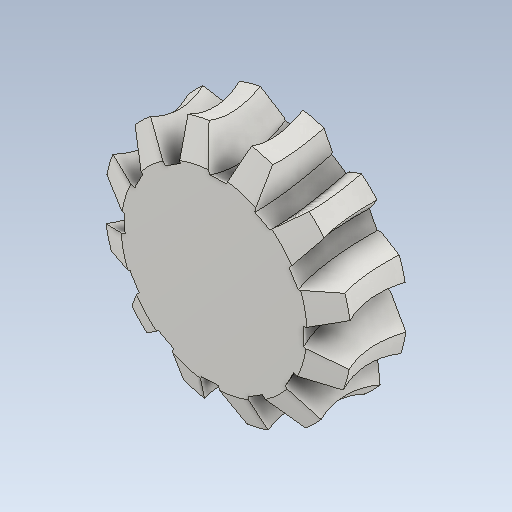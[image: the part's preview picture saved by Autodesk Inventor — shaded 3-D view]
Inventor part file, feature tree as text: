
AUTODESK INVENTOR PART (.ipt)
format: ipt  version: 2021 (Build 250183000, 183)  size: 323,072 bytes
history: native  units: mm (DEFAULTED — no unit token found)
features: other x8, plane x3, pattern_circular x1, sketch x1
ambient origin geometry x5: Origin, X Axis, Y Axis, Z Axis, Center Point
bodies: Solid1 (feature_tree)
feature tree (13):
  other  "Tooth Plane"
  other  "Base Body Sketch"
  other  "Base Body"
  other  "Base Body2"
  plane  "Work Plane13"
  other  "Tooth"
  pattern_circular  "Tooth Pattern"  [2 undecoded]
  plane  "Work Plane14"
  plane  "Work Plane15"
  other  "Tooth Sketch"
  sketch  "Sketch8"  dims[d35=90.0deg d37=-0.996687mm d38=44.0mm d39=3.490659mm d40=15.2mm d41=20.0mm d42=3.769911mm d43=90.0deg d44=120.0mm d46=360.0deg d50=4.297754mm d68=44.0mm d69=0.0mm d73=0.0mm d75=15.0deg d77=48.0mm d78=20.0mm d79=0.0mm d80=0.0mm d81=0.0mm d82=0.0mm d83=15.0deg d84=0.0mm d85=180.0deg d86=44.0mm d87=60.0mm d89=32.0mm d90=90.0deg d92=20.0mm d93=44.0mm]
  other  "Srf1"
  other  "Pitch Diameter"
note: 2 required parameter values undecoded (feature->parameter linkage not recoverable at this tier; creation-order binding heuristic only, values carry confidence <= 0.55)
